# Revit family: BC_Hitachi_Samurai-M-304050-LN_LOD400_
name_source: partatom
category: Mechanical Equipment
revit_build: Autodesk Revit 2018 (Build: 20170223_1515(x64)
units: mm (PartAtom-declared; Revit-internal decimal feet)

## family parameters
Always vertical = Yes
Classification = None
Cut with Voids When Loaded = No
Part Type = Normal
Room Calculation Point = No
Round Connector Dimension = Use Diameter
Shared = No
Work Plane-Based = No

## types (3) — shared parameters
BC_OBJECT_ID = 46958
BC_OBJECT_VERSION = #31
Description = Samurai M - Heat Pump Inverter Scroll (LN version) RHMA 18AN-N - RHMA 100AN-N
Frequency = 50 Hz
Inlet Water Diameter = 64 mm
Manufacturer = Hitachi Air Conditioning Europe SAS
MasterFormat = Central HVAC Equipment
Masterformat Code = 23 70 00
Model = Samurai M - Heat Pump Inverter Scroll (LN version)
Nominal Voltage = 400 V
Number of Poles = 3
OmniClass code = 23-33 21 13
OmniClass description = Chillers
Operating mode = Heating+Cooling
Overall height = 2440 mm
Overall length = 2240 mm
Overall width = 1200 mm
Refrigerant Type = R410A
Uniformat = Cooling Generating Systems
Uniformat code = D3030
Water Outlet Diameter = 64 mm

## per-type parameters (varying)
| type | Airflow (High) | BC_VARIANT_ID | Coefficient of Performance (COP) | Cooling Capacity | Cooling Input Rated | Energy efficiency SCOP | Energy efficiency ratio (EER) | Heating Capacity | Heating Input Rated | Load of Refrigerant Fluid | Packing Weight | Rated Cooling Current | SEER energy efficiency | Sound Power Low Noise (Cooling) | Sound Power Low Noise (Heating) | Sound Pressure at 10m (Cooling) | Sound Pressure at 1m (Cooling) | Starting current | Weight in operation |
| RHMA 30AN-N | 7668.9 L/s | 294247 | 3.15 | 75200 W | 24200 W | 3.4 | 3.11 | 83800 W | 26600 W | 17.60 kg | 919.00 kg | 44 A | 4.24 | 77 | 76 | 48 | 62 | 163 A | 893.00 kg |
| RHMA 40AN-N | 8679.7 L/s | 294248 | 3.07 | 92200 W | 30200 W | 3.35 | 3.05 | 90800 W | 29600 W | 20.50 kg | 944.00 kg | 56 A | 4.43 | 79 | 80 | 50 | 64 | 199 A | 920.00 kg |
| RHMA 50AN-N | 9965.8 L/s | 294249 | 2.85 | 117700 W | 40000 W | 3.39 | 2.94 | 124800 W | 43800 W | 22.80 kg | 1023.00 kg | 74 A | 4.37 | 80 | 81 | 51 | 65 | 212 A | 999.00 kg |

note: column(s) folded — value = type name in every type: Product Code, Reference
